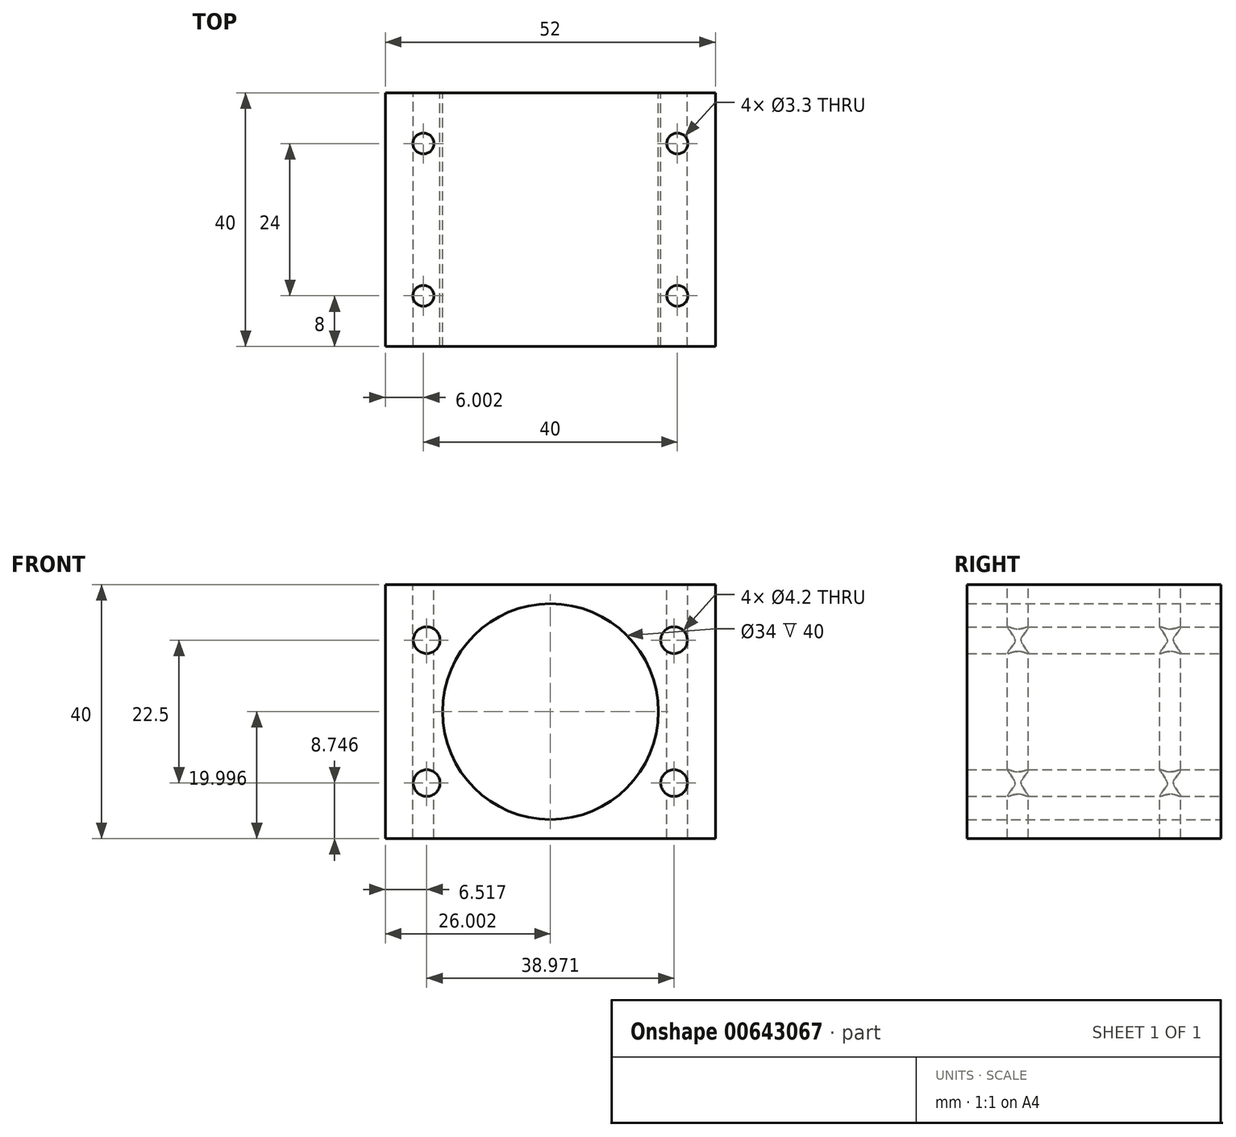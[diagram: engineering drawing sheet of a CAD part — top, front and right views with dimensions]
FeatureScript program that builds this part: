
annotation { "Feature Type Name" : "Feature", "Feature Type Description" : "" }
export const myFeature = defineFeature(function(context is Context, id is Id, definition is map)
    precondition{}
    {
        {
            var Q0;
            Q0=qCreatedBy(makeId("Front.planeOp"),FACE);
            var sketch = newSketch(context, id + "F0", { "sketchPlane" : qUnion([Q0])});
            skLineSegment(sketch, "E0.bottom", {"start": v(-23.76, 18.1) * mm, "end": v(28.24, 18.1) * mm});
            skLineSegment(sketch, "E0.top", {"start": v(-23.76, -21.9) * mm, "end": v(28.24, -21.9) * mm});
            skLineSegment(sketch, "E0.left", {"start": v(-23.76, 18.1) * mm, "end": v(-23.76, -21.9) * mm});
            skLineSegment(sketch, "E0.right", {"start": v(28.24, 18.1) * mm, "end": v(28.24, -21.9) * mm});
            skLineSegment(sketch, "E1", {"start": v(2.24, 18.1) * mm, "end": v(2.24, -21.9) * mm, "construction": true});
            skLineSegment(sketch, "E2", {"start": v(-23.76, -1.9) * mm, "end": v(28.24, -1.9) * mm, "construction": true});
            skCircle(sketch, "E3", {"center": v(2.24, -1.9) * mm, "radius": 17 * mm});
            skCircle(sketch, "E4", {"center": v(2.24, -1.9) * mm, "radius": 22.5 * mm, "construction": true});
            skPoint(sketch, "E5", {"position": v(-17.24, 9.35) * mm});
            skLineSegment(sketch, "E6", {"start": v(-17.24, 9.35) * mm, "end": v(2.24, -1.9) * mm, "construction": true});
            skPoint(sketch, "E7.MirrorP", {"position": v(21.73, 9.35) * mm});
            skPoint(sketch, "E8.MirrorP", {"position": v(-17.24, -13.15) * mm});
            skPoint(sketch, "E9.MirrorP", {"position": v(21.73, -13.15) * mm});
            skSolve(sketch);
        }
        {
            var Q0;
            Q0=makeQuery(id+"F0.imprint","IMPRINT",FACE,{"disambiguationData":[TD([[makeQuery(id+"F0.imprint","IMPRINT",EDGE,{"derivedFrom":sQuery(id+"F0.wireOp",EDGE,"E0.bottom")}),-1.0]])]});
            extrude(context, id + "F1", {"entities" : qUnion([Q0]), "depth" : 40 * mm});
        }
        {
            var Q0;
            Q0=sQuery(id+"F0.wireOp",VERTEX,"E7.MirrorP");
            var Q1;
            Q1=sQuery(id+"F0.wireOp",VERTEX,"E9.MirrorP");
            var Q2;
            Q2=sQuery(id+"F0.wireOp",VERTEX,"E8.MirrorP");
            var Q3;
            Q3=sQuery(id+"F0.wireOp",VERTEX,"E5");
            var Q4;
            Q4=makeQuery(id+"F1.opExtrude","SWEPT_BODY",BODY,{"disambiguationData":[OSD([sQuery(id+"F0.wireOp",EDGE,"E0.bottom"),sQuery(id+"F0.wireOp",EDGE,"E0.top"),sQuery(id+"F0.wireOp",EDGE,"E0.left"),sQuery(id+"F0.wireOp",EDGE,"E0.right"),sQuery(id+"F0.wireOp",EDGE,"E3")])]});
            hole(context, id + "F2", {"style" : HoleStyle.SIMPLE, "endStyle" : HoleEndStyle.THROUGH, "oppositeDirection" : true, "standardTappedOrClearance" : lookupTablePath({ "standard" : "ISO", "engagement" : "75%", "pitch" : "0.8 mm", "size" : "M5", "type" : "Tapped" }), "standardBlindInLast" : lookupTablePath({ "standard" : "ISO", "engagement" : "75%", "pitch" : "0.8 mm", "size" : "M5", "type" : "Tapped" }), "holeDiameter" : 4.2 * mm, "showTappedDepth" : true, "tappedDepth" : 12 * mm, "tapClearance" : 3, "locations" : qUnion([Q0, Q1, Q2, Q3]), "scope" : qUnion([Q4]), "majorDiameter" : 5 * mm});
        }
        {
            var Q0;
            Q0=makeQuery(id+"F1.opExtrude","SWEPT_FACE",FACE,{"disambiguationData":[OSD([sQuery(id+"F0.wireOp",EDGE,"E0.bottom")])]});
            var sketch = newSketch(context, id + "F3", { "sketchPlane" : qUnion([Q0])});
            skLineSegment(sketch, "E10", {"start": v(-23.76, -20) * mm, "end": v(28.24, -20) * mm, "construction": true});
            skLineSegment(sketch, "E11", {"start": v(2.24, 0) * mm, "end": v(2.24, -40) * mm, "construction": true});
            skPoint(sketch, "E12", {"position": v(-17.76, -8) * mm});
            skPoint(sketch, "E13.MirrorP", {"position": v(22.24, -8) * mm});
            skPoint(sketch, "E14.MirrorP", {"position": v(-17.76, -32) * mm});
            skPoint(sketch, "E15.MirrorP", {"position": v(22.24, -32) * mm});
            skSolve(sketch);
        }
        {
            var Q0;
            Q0=sQuery(id+"F3.wireOp",VERTEX,"E12");
            var Q1;
            Q1=sQuery(id+"F3.wireOp",VERTEX,"E14.MirrorP");
            var Q2;
            Q2=sQuery(id+"F3.wireOp",VERTEX,"E15.MirrorP");
            var Q3;
            Q3=sQuery(id+"F3.wireOp",VERTEX,"E13.MirrorP");
            var Q4;
            Q4=makeQuery(id+"F1.opExtrude","SWEPT_BODY",BODY,{"disambiguationData":[OSD([sQuery(id+"F0.wireOp",EDGE,"E0.bottom"),sQuery(id+"F0.wireOp",EDGE,"E0.top"),sQuery(id+"F0.wireOp",EDGE,"E0.left"),sQuery(id+"F0.wireOp",EDGE,"E0.right"),sQuery(id+"F0.wireOp",EDGE,"E3")])]});
            hole(context, id + "F4", {"style" : HoleStyle.SIMPLE, "endStyle" : HoleEndStyle.THROUGH, "standardTappedOrClearance" : lookupTablePath({ "standard" : "ISO", "engagement" : "75%", "pitch" : "0.7 mm", "size" : "M4", "type" : "Tapped" }), "standardBlindInLast" : lookupTablePath({ "standard" : "ISO", "engagement" : "75%", "pitch" : "0.7 mm", "size" : "M4", "type" : "Tapped" }), "holeDiameter" : 3.3 * mm, "showTappedDepth" : true, "tappedDepth" : 12 * mm, "tapClearance" : 3, "locations" : qUnion([Q0, Q1, Q2, Q3]), "scope" : qUnion([Q4]), "majorDiameter" : 4 * mm});
        }
    });
